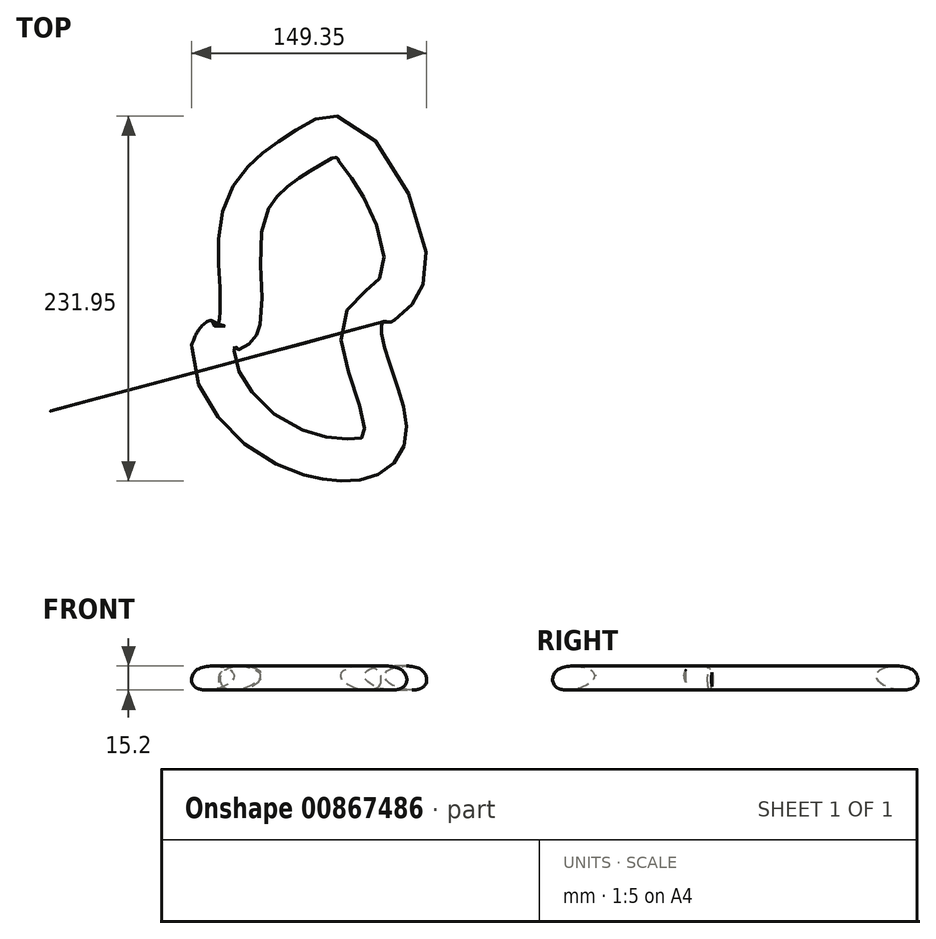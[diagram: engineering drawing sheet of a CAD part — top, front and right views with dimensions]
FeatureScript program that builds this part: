
annotation { "Feature Type Name" : "Feature", "Feature Type Description" : "" }
export const myFeature = defineFeature(function(context is Context, id is Id, definition is map)
    precondition{}
    {
        {
            var Q0;
            Q0=qCreatedBy(makeId("Top.planeOp"),FACE);
            var sketch = newSketch(context, id + "F0", { "sketchPlane" : qUnion([Q0])});
            skFitSpline(sketch, "E0", {"points": [v(-55.92, 0) * mm, v(-23.14, -52.7) * mm, v(42.56, -57.6) * mm, v(29.61, 12.88) * mm, v(55.87, 47.7) * mm, v(21.4, 126.85) * mm, v(0, 122.91) * mm, v(-37.63, 84.34) * mm, v(-42.06, 12.94) * mm, v(-55.92, 0) * mm]});
            skSolve(sketch);
        }
        {
            var Q0;
            Q0=qCreatedBy(makeId("Front.planeOp"),FACE);
            var sketch = newSketch(context, id + "F1", { "sketchPlane" : qUnion([Q0])});
            skFitSpline(sketch, "E1", {"points": [v(-72.87, -13.66) * mm, v(-70.77, -2.87) * mm, v(-46.53, -5) * mm, v(-51.1, -12.64) * mm, v(-72.87, -13.66) * mm]});
            skSolve(sketch);
        }
        {
            var Q0;
            Q0=makeQuery(id+"F1.imprint","IMPRINT",FACE,{"disambiguationData":[TD([[makeQuery(id+"F1.imprint","IMPRINT",EDGE,{"derivedFrom":sQuery(id+"F1.wireOp",EDGE,"E1")}),-1.0]])]});
            var Q1;
            Q1=sQuery(id+"F0.wireOp",EDGE,"E0");
            sweep(context, id + "F2", {"profiles" : qUnion([Q0]), "path" : qUnion([Q1])});
        }
    });
